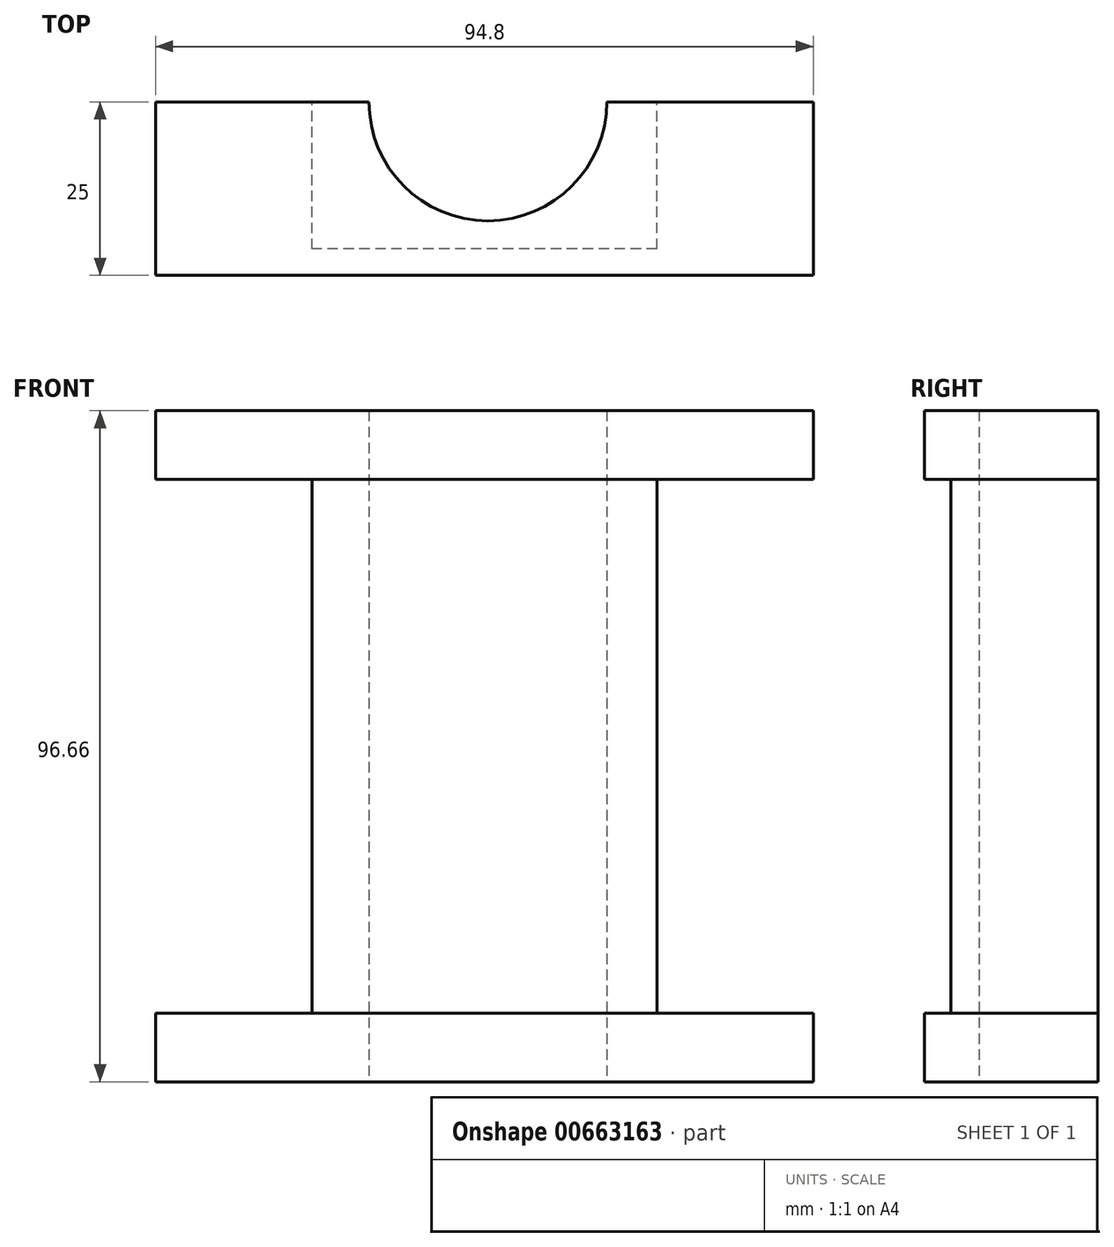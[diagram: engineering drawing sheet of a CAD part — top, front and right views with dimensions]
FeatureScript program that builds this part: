
annotation { "Feature Type Name" : "Feature", "Feature Type Description" : "" }
export const myFeature = defineFeature(function(context is Context, id is Id, definition is map)
    precondition{}
    {
        {
            var Q0;
            Q0=qCreatedBy(makeId("Front.planeOp"),FACE);
            var sketch = newSketch(context, id + "F0", { "sketchPlane" : qUnion([Q0])});
            skLineSegment(sketch, "E0", {"start": v(-47.4, 48.33) * mm, "end": v(0, 48.33) * mm});
            skLineSegment(sketch, "E1", {"start": v(-47.4, 48.33) * mm, "end": v(-47.4, 38.44) * mm});
            skLineSegment(sketch, "E2", {"start": v(-47.4, 38.44) * mm, "end": v(-24.86, 38.44) * mm});
            skLineSegment(sketch, "E3", {"start": v(-24.86, 38.44) * mm, "end": v(-24.86, 0) * mm});
            skLineSegment(sketch, "E4.MirrorCS", {"start": v(47.4, 48.33) * mm, "end": v(0, 48.33) * mm});
            skLineSegment(sketch, "E5.MirrorCS", {"start": v(47.4, 48.33) * mm, "end": v(47.4, 38.44) * mm});
            skLineSegment(sketch, "E6.MirrorCS", {"start": v(47.4, 38.44) * mm, "end": v(24.86, 38.44) * mm});
            skLineSegment(sketch, "E7.MirrorCS", {"start": v(24.86, 38.44) * mm, "end": v(24.86, 0) * mm});
            skLineSegment(sketch, "E8.MirrorCS", {"start": v(-24.86, -38.44) * mm, "end": v(-24.86, 0) * mm});
            skLineSegment(sketch, "E9.MirrorCS", {"start": v(-47.4, -38.44) * mm, "end": v(-24.86, -38.44) * mm});
            skLineSegment(sketch, "E10.MirrorCS", {"start": v(-47.4, -48.33) * mm, "end": v(-47.4, -38.44) * mm});
            skLineSegment(sketch, "E11.MirrorCS", {"start": v(-47.4, -48.33) * mm, "end": v(0, -48.33) * mm});
            skLineSegment(sketch, "E12.MirrorCS", {"start": v(47.4, -48.33) * mm, "end": v(0, -48.33) * mm});
            skLineSegment(sketch, "E13.MirrorCS", {"start": v(47.4, -38.44) * mm, "end": v(24.86, -38.44) * mm});
            skLineSegment(sketch, "E14.MirrorCS", {"start": v(47.4, -48.33) * mm, "end": v(47.4, -38.44) * mm});
            skLineSegment(sketch, "E15.MirrorCS", {"start": v(24.86, -38.44) * mm, "end": v(24.86, 0) * mm});
            skSolve(sketch);
        }
        {
            var Q0;
            Q0=makeQuery(id+"F0.imprint","IMPRINT",FACE,{"disambiguationData":[TD([[makeQuery(id+"F0.imprint","IMPRINT",EDGE,{"derivedFrom":sQuery(id+"F0.wireOp",EDGE,"E0")}),-1.0]])]});
            extrude(context, id + "F1", {"entities" : qUnion([Q0]), "depth" : 25 * mm, "offsetDistance" : 25 * mm});
        }
        {
            var Q0;
            Q0=makeQuery(id+"F1.opExtrude","CAP_FACE",FACE,{"disambiguationData":[OSD([sQuery(id+"F0.wireOp",EDGE,"E0"),sQuery(id+"F0.wireOp",EDGE,"E1"),sQuery(id+"F0.wireOp",EDGE,"E2"),sQuery(id+"F0.wireOp",EDGE,"E3"),sQuery(id+"F0.wireOp",EDGE,"E4.MirrorCS"),sQuery(id+"F0.wireOp",EDGE,"E5.MirrorCS"),sQuery(id+"F0.wireOp",EDGE,"E6.MirrorCS"),sQuery(id+"F0.wireOp",EDGE,"E7.MirrorCS"),sQuery(id+"F0.wireOp",EDGE,"E8.MirrorCS"),sQuery(id+"F0.wireOp",EDGE,"E9.MirrorCS"),sQuery(id+"F0.wireOp",EDGE,"E10.MirrorCS"),sQuery(id+"F0.wireOp",EDGE,"E11.MirrorCS"),sQuery(id+"F0.wireOp",EDGE,"E12.MirrorCS"),sQuery(id+"F0.wireOp",EDGE,"E13.MirrorCS"),sQuery(id+"F0.wireOp",EDGE,"E14.MirrorCS"),sQuery(id+"F0.wireOp",EDGE,"E15.MirrorCS")])],"isStart":false});
            var sketch = newSketch(context, id + "F2", { "sketchPlane" : qUnion([Q0])});
            skLineSegment(sketch, "E16", {"start": v(24.86, -38.44) * mm, "end": v(-24.86, -38.44) * mm});
            skLineSegment(sketch, "E17", {"start": v(-24.86, -38.44) * mm, "end": v(-24.86, 38.44) * mm});
            skLineSegment(sketch, "E18", {"start": v(-24.86, 38.44) * mm, "end": v(24.86, 38.44) * mm});
            skLineSegment(sketch, "E19", {"start": v(24.86, 38.44) * mm, "end": v(24.86, -38.44) * mm});
            skSolve(sketch);
        }
        {
            var Q0;
            Q0=makeQuery(id+"F2.imprint","IMPRINT",FACE,{"disambiguationData":[TD([[makeQuery(id+"F2.imprint","IMPRINT",EDGE,{"derivedFrom":sQuery(id+"F2.wireOp",EDGE,"E16")}),-1.0]])]});
            extrude(context, id + "F3", {"entities" : qUnion([Q0]), "operationType" : NewBodyOperationType.REMOVE, "oppositeDirection" : true, "depth" : 3.8 * mm, "offsetDistance" : 25 * mm});
        }
        {
            var Q0;
            Q0=makeQuery(id+"F1.opExtrude","SWEPT_FACE",FACE,{"disambiguationData":[OSD([sQuery(id+"F0.wireOp",EDGE,"E11.MirrorCS"),sQuery(id+"F0.wireOp",EDGE,"E12.MirrorCS")])]});
            var sketch = newSketch(context, id + "F4", { "sketchPlane" : qUnion([Q0])});
            skLineSegment(sketch, "E20", {"start": v(17.63, 0) * mm, "end": v(-16.65, 0) * mm});
            skArc(sketch, "E21", {"start": v(17.63, 0) * mm, "mid": v(0.49, 17.14) * mm, "end": v(-16.65, 0) * mm});
            skSolve(sketch);
        }
        {
            var Q0;
            Q0=makeQuery(id+"F4.imprint","IMPRINT",FACE,{"disambiguationData":[TD([[makeQuery(id+"F4.imprint","IMPRINT",EDGE,{"derivedFrom":sQuery(id+"F4.wireOp",EDGE,"E20")}),1.0]])]});
            extrude(context, id + "F5", {"entities" : qUnion([Q0]), "operationType" : NewBodyOperationType.REMOVE, "oppositeDirection" : true, "depth" : 97.5 * mm, "offsetDistance" : 25 * mm});
        }
    });
